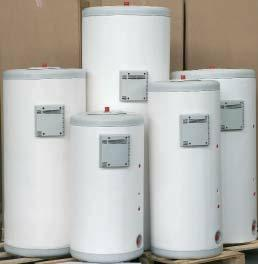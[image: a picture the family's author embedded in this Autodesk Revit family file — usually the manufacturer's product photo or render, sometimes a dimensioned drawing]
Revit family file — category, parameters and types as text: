
# Revit family: CV-150-M1S_CC01703
name_source: partatom
category: Aparatos eléctricos
revit_build: Autodesk Revit 2016 (Build: 20150220_1215(x64)
units: mm (PartAtom-declared; Revit-internal decimal feet)

## family parameters
Compartido = No
Corte con vacíos al cargar = No
Número OmniClass = 23.80.00.00
Punto de cálculo de habitación = No
Se basa en plano de trabajo = No
Siempre vertical = Sí
Título OmniClass = Electric Power and Lighting

## types (1)
- Interacumuladores CV-M1S
    Clase eficiencia energética = B
    Costo = 0 $
    Código de montaje = CC01703
    Descripción = INTERACUMULADOR CON SERPENTIN FIJO
    Dimensiones = 560 x 1260 mm
    Fabricante = SALVADOR ESCODA
    Imagen de tipo = CV-M1S.jpg
    Modelo = CV 150 M1S
    Peso vacío (aprox.) = 60 Kg
    Presión máx. depósito = 8 bar
    Pérdidas estáticas = 44 W
    Superfície intercambiador = 0,6 m2
    Temperatura máx. ACS = 90 ºC
    Temperatura máx. circuito calentamiento = 200 ºC
    URL = www.salvadorescoda.com
    Volúmen = 150 l
